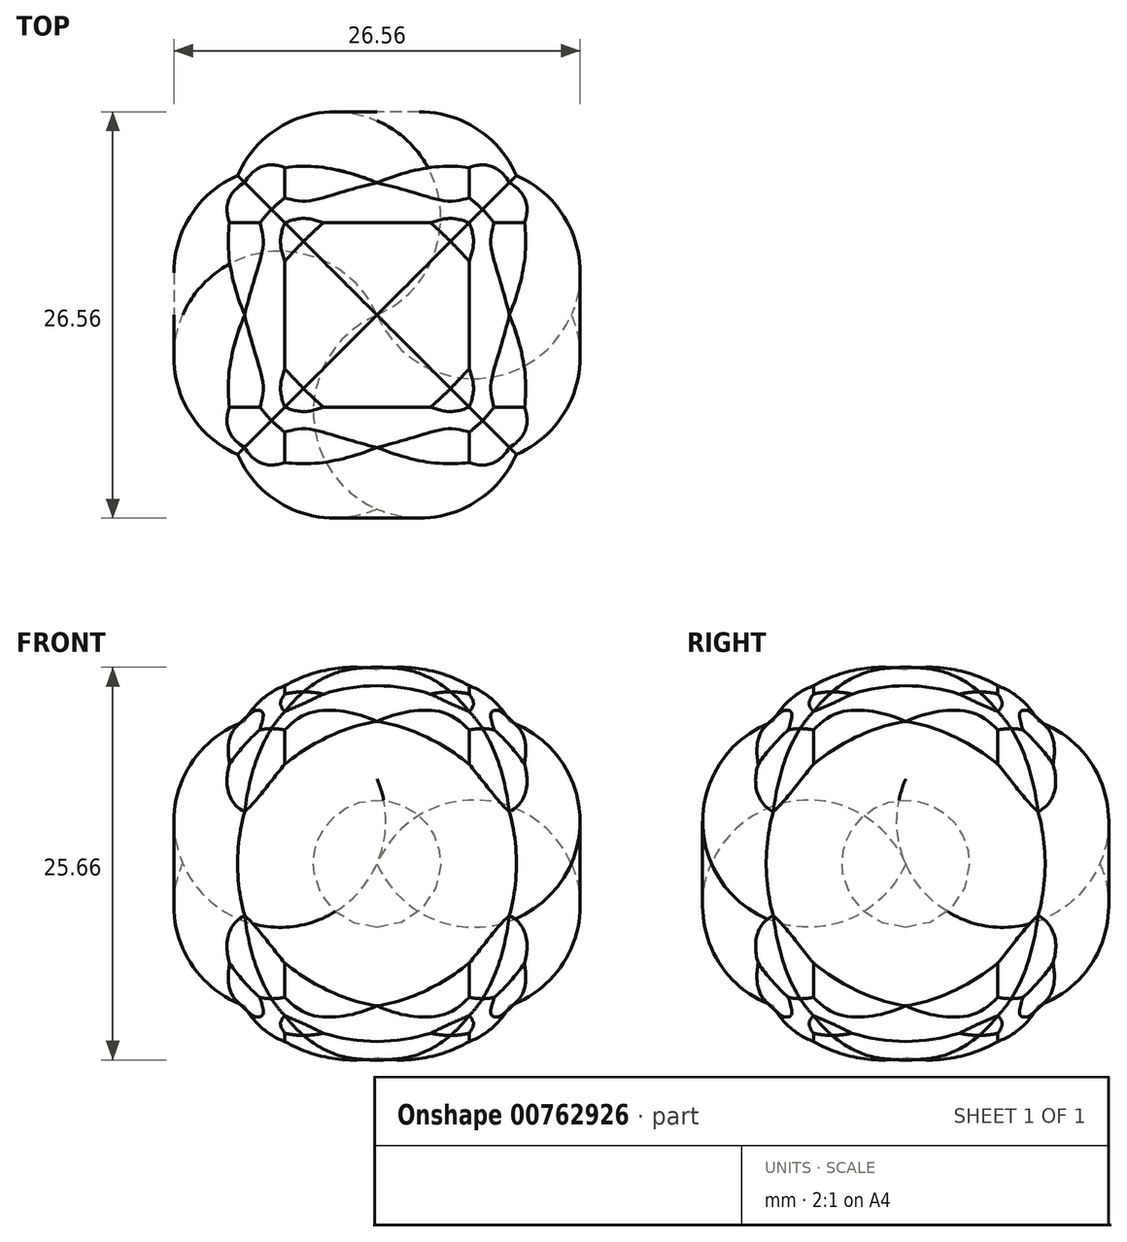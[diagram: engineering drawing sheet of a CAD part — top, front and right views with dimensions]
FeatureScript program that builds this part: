
annotation { "Feature Type Name" : "Feature", "Feature Type Description" : "" }
export const myFeature = defineFeature(function(context is Context, id is Id, definition is map)
    precondition{}
    {
        {
            var Q0;
            Q0=qCreatedBy(makeId("Top.planeOp"),FACE);
            var sketch = newSketch(context, id + "F0", { "sketchPlane" : qUnion([Q0])});
            skArc(sketch, "E0.trimOffspring", {"start": v(-8.65, 9.3) * mm, "mid": v(-12.7, 5.53) * mm, "end": v(-12.7, 0) * mm});
            skPoint(sketch, "E1.end.orphan", {"position": v(0, 12.7) * mm});
            skArc(sketch, "E2", {"start": v(-6.03, 11.62) * mm, "mid": v(-7.56, 10.7) * mm, "end": v(-8.65, 9.3) * mm});
            skArc(sketch, "E3", {"start": v(0, 12.7) * mm, "mid": v(-3.1, 12.7) * mm, "end": v(-6.03, 11.62) * mm});
            skLineSegment(sketch, "E4", {"start": v(-12.7, 0) * mm, "end": v(0, 0) * mm});
            skArc(sketch, "E5.MirrorCS", {"start": v(8.65, 9.3) * mm, "mid": v(12.7, 5.53) * mm, "end": v(12.7, 0) * mm});
            skArc(sketch, "E6.MirrorCS", {"start": v(6.03, 11.62) * mm, "mid": v(7.56, 10.7) * mm, "end": v(8.65, 9.3) * mm});
            skArc(sketch, "E7.MirrorCS", {"start": v(0, 12.7) * mm, "mid": v(3.1, 12.7) * mm, "end": v(6.03, 11.62) * mm});
            skLineSegment(sketch, "E8.MirrorCS", {"start": v(12.7, 0) * mm, "end": v(0, 0) * mm});
            skSolve(sketch);
        }
        {
            var Q0;
            Q0=makeQuery(id+"F0.imprint","IMPRINT",FACE,{"disambiguationData":[TD([[makeQuery(id+"F0.imprint","IMPRINT",EDGE,{"derivedFrom":sQuery(id+"F0.wireOp",EDGE,"E0.trimOffspring")}),1.0]])]});
            var Q1;
            Q1=sQuery(id+"F0.wireOp",EDGE,"E4");
            revolve(context, id + "F1", {"surfaceOperationType" : NewSurfaceOperationType.NEW, "entities" : qUnion([Q0]), "axis" : qUnion([Q1]), "revolveType" : RevolveType.FULL});
        }
        {
            var Q0;
            Q0=qCreatedBy(makeId("Top.planeOp"),FACE);
            var sketch = newSketch(context, id + "F2", { "sketchPlane" : qUnion([Q0])});
            skLineSegment(sketch, "E9", {"start": v(0, 12.7) * mm, "end": v(0, 0) * mm});
            skArc(sketch, "E10.trimOffspring", {"start": v(9.3, 8.65) * mm, "mid": v(5.53, 12.7) * mm, "end": v(0, 12.7) * mm});
            skPoint(sketch, "E11.end.orphan", {"position": v(12.7, 0) * mm});
            skArc(sketch, "E12", {"start": v(11.62, 6.03) * mm, "mid": v(10.7, 7.56) * mm, "end": v(9.3, 8.65) * mm});
            skArc(sketch, "E13", {"start": v(12.7, 0) * mm, "mid": v(12.7, 3.1) * mm, "end": v(11.62, 6.03) * mm});
            skPoint(sketch, "E14.end.orphan", {"position": v(9.3, -8.65) * mm});
            skArc(sketch, "E15.MirrorCS", {"start": v(11.62, -6.03) * mm, "mid": v(10.7, -7.56) * mm, "end": v(9.3, -8.65) * mm});
            skArc(sketch, "E16.MirrorCS", {"start": v(9.3, -8.65) * mm, "mid": v(5.53, -12.7) * mm, "end": v(0, -12.7) * mm});
            skArc(sketch, "E17.MirrorCS", {"start": v(12.7, 0) * mm, "mid": v(12.7, -3.1) * mm, "end": v(11.62, -6.03) * mm});
            skLineSegment(sketch, "E18.MirrorCS", {"start": v(0, -12.7) * mm, "end": v(0, 0) * mm});
            skSolve(sketch);
        }
        {
            var Q0;
            Q0=makeQuery(id+"F2.imprint","IMPRINT",FACE,{"disambiguationData":[TD([[makeQuery(id+"F2.imprint","IMPRINT",EDGE,{"derivedFrom":sQuery(id+"F2.wireOp",EDGE,"E9")}),1.0]])]});
            var Q1;
            Q1=sQuery(id+"F2.wireOp",EDGE,"E9");
            revolve(context, id + "F3", {"operationType" : NewBodyOperationType.ADD, "surfaceOperationType" : NewSurfaceOperationType.NEW, "entities" : qUnion([Q0]), "axis" : qUnion([Q1]), "revolveType" : RevolveType.FULL});
        }
    });
